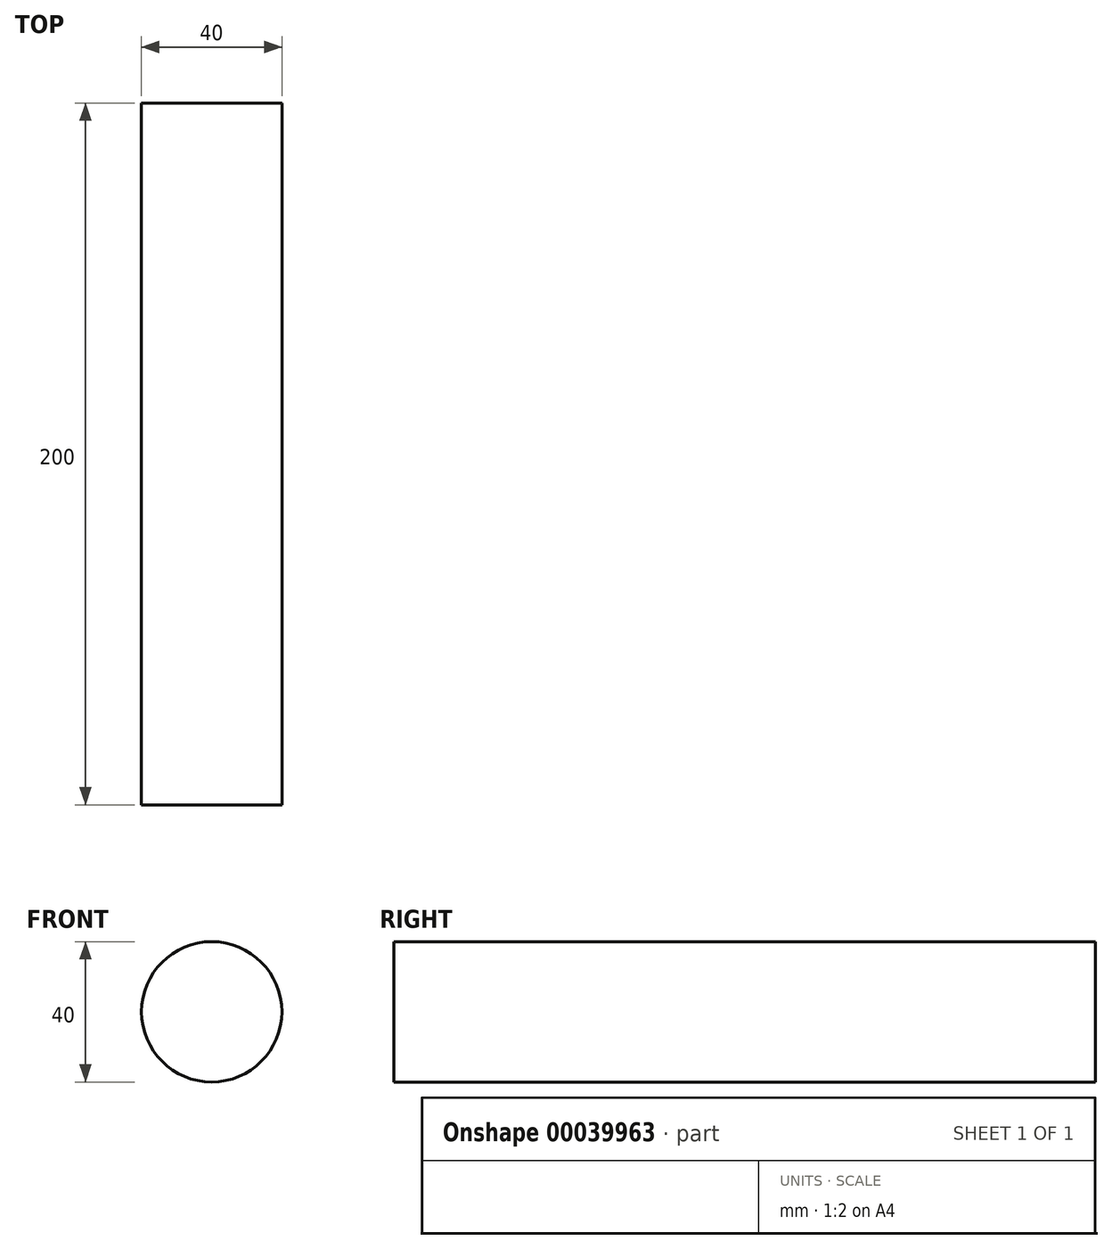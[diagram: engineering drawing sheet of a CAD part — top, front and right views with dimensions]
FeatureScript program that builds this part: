
annotation { "Feature Type Name" : "Feature", "Feature Type Description" : "" }
export const myFeature = defineFeature(function(context is Context, id is Id, definition is map)
    precondition{}
    {
        {
            var Q0;
            Q0=qCreatedBy(makeId("Front.planeOp"),FACE);
            var sketch = newSketch(context, id + "F0", { "sketchPlane" : qUnion([Q0])});
            skCircle(sketch, "E0", {"center": v(0, 0) * mm, "radius": 20 * mm});
            skSolve(sketch);
        }
        {
            var Q0;
            Q0=makeQuery(id+"F0.imprint","IMPRINT",FACE,{"disambiguationData":[TD([[makeQuery(id+"F0.imprint","IMPRINT",EDGE,{"derivedFrom":sQuery(id+"F0.wireOp",EDGE,"E0")}),1.0]])]});
            extrude(context, id + "F1", {"entities" : qUnion([Q0]), "endBound" : BoundingType.SYMMETRIC, "depth" : 200 * mm});
        }
    });
